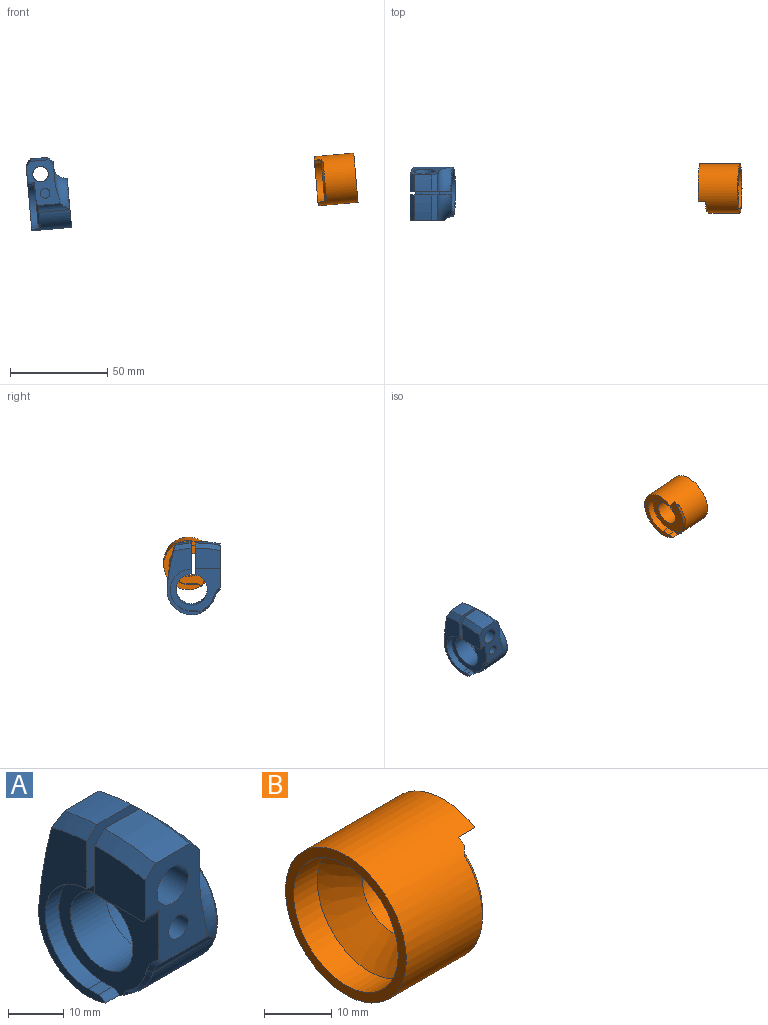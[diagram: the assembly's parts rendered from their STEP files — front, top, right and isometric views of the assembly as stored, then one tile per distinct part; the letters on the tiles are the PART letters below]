
ASSEMBLY  parts=2 mates=1
PART A: 37 faces, bbox 27.2x53.3x40.6 mm
  f0: cylinder r=5.5mm len=11mm, axis (0,1,0), area 68.2mm2, adj f10,f24
  f1: cylinder r=4mm len=13mm, axis (0,-1,0), area 326.7mm2, adj f11,f22
  f2: cylinder r=2.5mm len=5mm, axis (0,-1,0), area 62.8mm2, adj f11,f21
  f3: cylinder r=11mm len=22mm, axis (1,0,0), area 536.9mm2, adj f14,f20,f22,f23
  f4: cylinder r=4mm len=8mm, axis (0,-1,0), area 201.1mm2, adj f23,f24
  f5: cylinder r=54.32mm len=13mm, axis (-1,0,0), area 116.8mm2, adj f11,f22,f30,f33
  f6: cylinder r=12.7mm len=25.4mm, axis (-1,0,0), area 722mm2, adj f7,f9,f10,f12,f14,f18,f22,f23
  f7: plane 25.7x23.86mm, normal (-1,0,0), area 255.6mm2, adj f6,f11,f13,f16,f17,f18,f19,f22
  f8: cylinder r=54.32mm len=8.92mm, axis (-1,0,0), area 75.3mm2, adj f10,f23,f31,f32
  f9: cylinder r=6.48mm len=15.85mm, axis (-1,0,0), area 59.4mm2, adj f6,f11,f27,f36
  f10: cylinder r=115.42mm len=21.88mm, axis (-1,0,0), area 255.3mm2, adj f0,f6,f8,f12,f25,f28,f31,f32
  f11: plane 25.31x18.09mm, normal (0,-1,0), area 212.4mm2, adj f1,f2,f5,f7,f9,f15,f26,f27
  f12: plane 34.34x17.24mm, normal (-1,0,0), area 177.6mm2, adj f6,f10,f16,f18,f19,f23,f32
  f13: cylinder r=8mm len=16mm, axis (-1,0,0), area 434.3mm2, adj f7,f20,f22,f23
  f14: plane 25.4x25.4mm, normal (1,0,0), area 123.2mm2, adj f3,f6,f22,f23
  f15: plane 13x10.74mm, normal (-1,0,0), area 134.3mm2, adj f11,f17,f22,f29,f33
  f16: cylinder r=11mm len=22mm, axis (-1,0,0), area 119.9mm2, adj f7,f12,f19,f23
  f17: plane 12x3.5mm, normal (0,0,-1), area 42mm2, adj f7,f15,f22,f29
  f18: cylinder r=2.5mm len=3.5mm, axis (-1,0,0), area 7.5mm2, adj f6,f7,f12,f19
  f19: plane 3.5x2.65mm, normal (0,0,1), area 9.3mm2, adj f7,f12,f16,f18
  f20: plane 22x22mm, normal (1,0,0), area 173mm2, adj f3,f13,f22,f23
  f21: plane 5x5mm, normal (0,-1,0), area 19.6mm2, adj f2
  f22: plane 20.68x16.56mm, normal (0,1,0), area 177mm2, adj f1,f3,f5,f6,f7,f13,f14,f15
  f23: plane 20.53x16.16mm, normal (0,-1,0), area 173.9mm2, adj f3,f4,f6,f7,f8,f12,f13,f14
  f24: plane 11x11mm, normal (0,1,0), area 44.8mm2, adj f0,f4
  f25: plane 10.11x5.68mm, normal (1,0,0), area 27.9mm2, adj f10,f23,f28,f31
  f26: plane 13x9.63mm, normal (1,0,0), area 60.8mm2, adj f11,f22,f27,f30
  f27: torus R=19.05mm, axis (1,0,0), area 199.2mm2, adj f6,f9,f11,f22,f26
  f28: torus R=19.05mm, axis (1,0,0), area 146.6mm2, adj f6,f10,f23,f25
  f29: cylinder r=1mm len=3.5mm, axis (-1,0,0), area 5.5mm2, adj f7,f11,f15,f17
  f30: revolved ~13.64x3.81mm, area 46.5mm2, adj f5,f11,f22,f26
  f31: revolved ~10.94x3.88mm, area 31.4mm2, adj f8,f10,f23,f25
  f32: revolved ~10.94x3.88mm, area 31.4mm2, adj f8,f10,f12,f23
  f33: revolved ~13.64x3.81mm, area 46.5mm2, adj f5,f11,f15,f22
  f34: revolved ~2.57x1.67mm, area 1.6mm2, adj f6,f7,f35
  f35: revolved ~7.74x5.01mm, area 10.9mm2, adj f6,f7,f34,f36
  f36: revolved ~4.51x3.12mm, area 6.1mm2, adj f7,f9,f11,f35
PART B: 15 faces, bbox 20.5x25.4x25.4 mm
  f0: cone r=6.25mm half-angle=45deg, axis (-1,0,0), area 364mm2, adj f1,f2
  f1: cylinder r=11mm len=22mm, axis (-1,0,0), area 345.6mm2, adj f0,f5
  f2: cylinder r=6.25mm len=12.5mm, axis (-1,0,0), area 284.7mm2, adj f0,f4
  f3: cylinder r=12.7mm len=25.4mm, axis (-1,0,0), area 1525.2mm2, adj f4,f5,f6,f7,f8,f12,f13,f14
  f4: plane 21.76x21.64mm, normal (1,0,0), area 241.2mm2, adj f2,f3,f7,f8,f9,f10,f11,f12
  f5: plane 25.4x25.4mm, normal (-1,0,0), area 126.6mm2, adj f1,f3
  f6: plane 25.4x19.35mm, normal (1,0,0), area 122.9mm2, adj f3,f7,f8,f9,f10,f11
  f7: cylinder r=3.61mm len=3.5mm, axis (1,0,0), area 8.7mm2, adj f3,f4,f6,f9
  f8: cylinder r=3.61mm len=3.5mm, axis (1,0,0), area 8.7mm2, adj f3,f4,f6,f11
  f9: plane 4.36x3.5mm, normal (0,0,-1), area 15.2mm2, adj f4,f6,f7,f10
  f10: cylinder r=10mm len=20mm, axis (1,0,0), area 110mm2, adj f4,f6,f9,f11
  f11: plane 4.36x3.5mm, normal (0,0,1), area 15.2mm2, adj f4,f6,f8,f10
  f12: cone r=2.19mm half-angle=45deg, axis (1,0,0), area 1.1mm2, adj f3,f4,f13
  f13: cone r=11.76mm half-angle=45deg, axis (-1,0,0), area 25mm2, adj f3,f4,f12,f14
  f14: cone r=2.19mm half-angle=45deg, axis (1,0,0), area 1.1mm2, adj f3,f4,f13
PLACE A rot(axis=(0,-1,0),5deg) t=(-104.5,169.06,-50.16)mm
PLACE B rot(axis=(0,1,0),175deg) t=(63.36,170.77,-35.47)mm
MATE parallel A.f3 <-> B.f4  axis (-1,0,-0.09) through (-101.01,169.06,-49.85)mm
